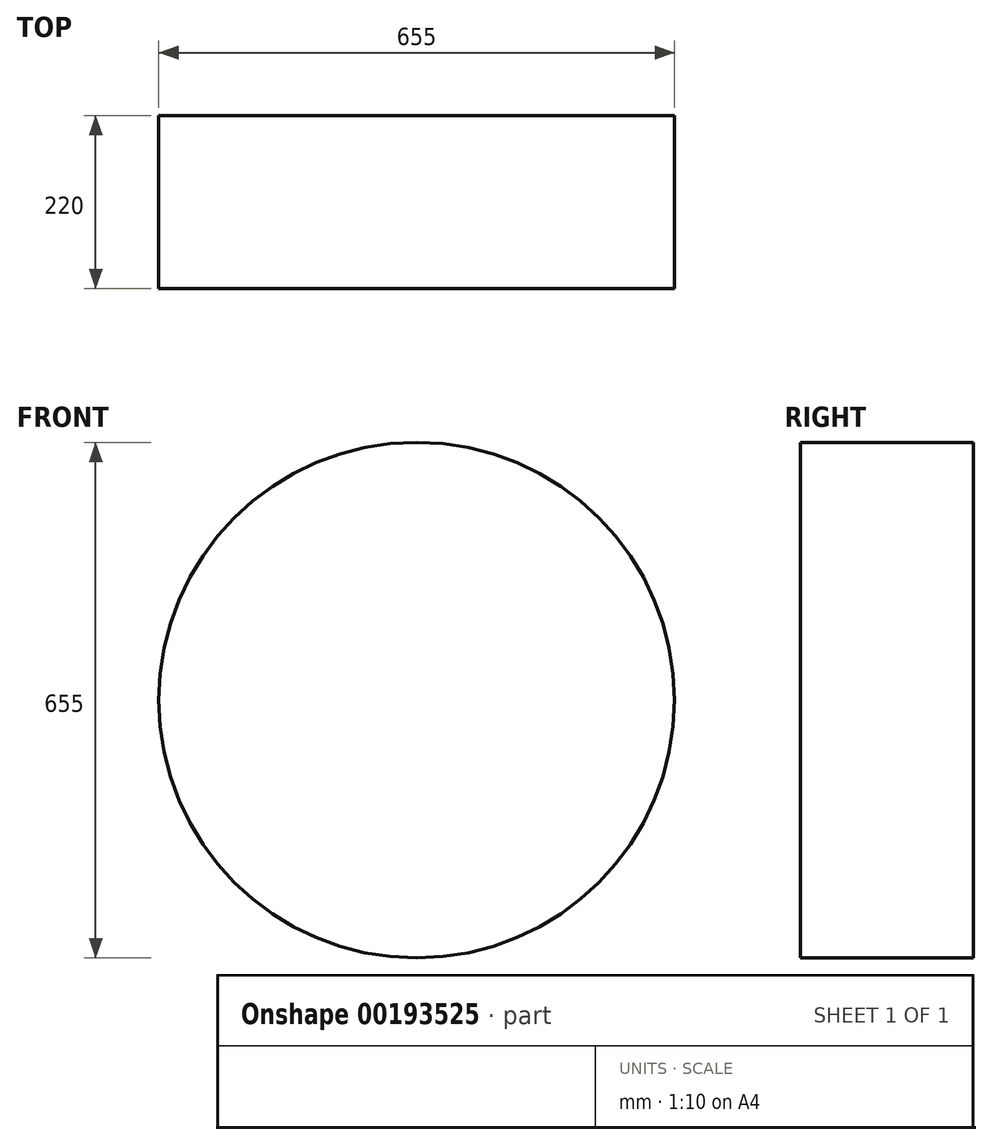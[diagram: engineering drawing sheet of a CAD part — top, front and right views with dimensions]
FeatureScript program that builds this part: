
annotation { "Feature Type Name" : "Feature", "Feature Type Description" : "" }
export const myFeature = defineFeature(function(context is Context, id is Id, definition is map)
    precondition{}
    {
        {
            var Q0;
            Q0=qCreatedBy(makeId("Front.planeOp"),FACE);
            var sketch = newSketch(context, id + "F0", { "sketchPlane" : qUnion([Q0])});
            skCircle(sketch, "E0", {"center": v(0, 0) * mm, "radius": 327.5 * mm});
            skSolve(sketch);
        }
        {
            var Q0;
            Q0=makeQuery(id+"F0.imprint","IMPRINT",FACE,{"disambiguationData":[TD([[makeQuery(id+"F0.imprint","IMPRINT",EDGE,{"derivedFrom":sQuery(id+"F0.wireOp",EDGE,"E0")}),1.0]])]});
            extrude(context, id + "F1", {"entities" : qUnion([Q0]), "depth" : 220 * mm});
        }
    });
